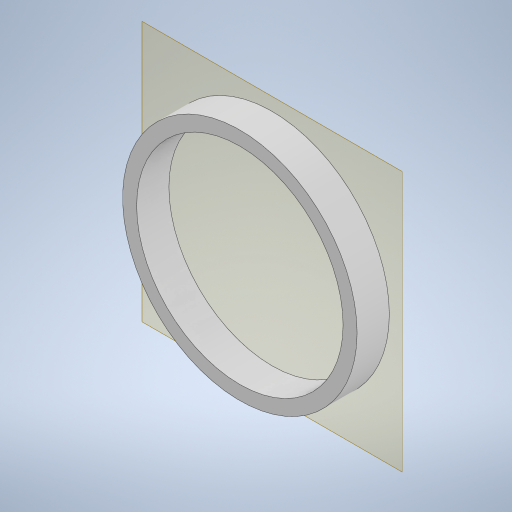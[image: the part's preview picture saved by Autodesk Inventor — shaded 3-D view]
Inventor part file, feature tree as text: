
AUTODESK INVENTOR PART (.ipt)
format: ipt  version: 2024 (Build 280153000, 153)  size: 582,656 bytes
history: native  units: mm
features: other x4, reference x3, plane x1, extrude x1, sketch x1
ambient origin geometry x8: Origin, YZ Plane, XZ Plane, XY Plane, X Axis, Y Axis, Z Axis, Center Point
bodies: Solid1 (feature_tree)
feature tree (10):
  plane  "Work Plane1"
  extrude  "Extrusion1"  Depth=6.0mm
  sketch  "Sketch1"  dims[d0=0.2mm d1=0.2mm d2=6.0mm d3=0.0mm]
  reference  "Reference1"
  reference  "Reference2"
  reference  "Reference3"
  other  "<userpath>\Documents\Inventor\robot arm\arms\arms.iam"
  other  "arms.iam"
  other  "arm-bearings:6"
  other  "arm middle:1"
